# Revit family: Haworth_Very_Stool_SeminarStarBase_EU_PRELIMINARY
name_source: partatom
category: Furniture
revit_build: Autodesk Revit 2018 (Build: 20170223_1515(x64)
units: mm (PartAtom-declared; Revit-internal decimal feet)

## family parameters
Always vertical = Yes
Cut with Voids When Loaded = No
OmniClass Number = 23.40.70.14.64.21
OmniClass Title = Systems Furniture
Room Calculation Point = No
Shared = No
Work Plane-Based = No

## types (6) — shared parameters
Actual Depth = 68 cm
Actual Height = 111 cm
Actual Width = 56 cm
Arm Cap Finish = Haworth _ Polymer _ Slate
Assembly Code = E2020200
Caster Finish = Haworth _ Paint _ Black
Description = Haworth - Very - Stool - Seminar
Manufacturer = Haworth
Model = 621X
Revision Number = 1
Size = Verify Final Dim. w/ Haworth
Sustainability Info = https://www.haworth.com
URL = https://www.haworth.com
URL - Product = https://www.haworth.com
Warranty = http://www.haworth.com

## per-type parameters (varying)
| type | Arms | Back Cushion | Seat Cushion |
| with Arm, with both Cushion | Yes | Yes | Yes |
| with Arm, with seat Cushion | Yes | No | Yes |
| with Arm, without Cushion | Yes | No | No |
| without Arm, with both Cushion | No | Yes | Yes |
| without Arm, with seat Cushion | No | No | Yes |
| without Arm, without Cushion | No | No | No |

## geometry (parser evidence)
native form markers: Sweep x21
no freeform markers — native parametric forms only
